# Revit family: HOSPIVAC V3 E65-300
name_source: partatom
category: Equipement de génie climatique
revit_build: Autodesk Revit 2018 (Build: 20170223_1515(x64)
units: mm (PartAtom-declared; Revit-internal decimal feet)

## family parameters
Basée sur le plan de construction = Non
Classification = Aucun
Cote de connecteur circulaire = Utiliser le diamètre
Couper avec des vides une fois chargée = Non
Partagée = Non
Point de calcul de pièce = Non
Toujours verticalement = Oui
Type d'élément = Normal

## types (5) — shared parameters
COS_PHI = 0.9
DIAM_ASPI_VIDE = 32 mm  [stored 0.104987 ft]
DIAM_REFOUL_VIDE = 40 mm  [stored 0.131234 ft]
DOUBLE_ALIMENTATION = Oui
FREQUENCE = 50 Hz
Fabricant = MIL'S
Lien espace client = https://www.mils.fr
Modèle = HOSPIVAC V3 EVISA
NBR_POLES = 3
NEUTRE = Oui
OFFSET_HAUT_ASPI = 895 mm  [stored 2.93635 ft]
OFFSET_HAUT_REFOUL = 410 mm  [stored 1.34514 ft]
TENSION_ALIM = 400 V
TERRE = Oui
Zone de maintenance 1 = Oui

## per-type parameters (varying)
- a - HOSPIVAC V3 E65: DEBIT_ASPI_VIDE=204.0 m³/h; DEBIT_REFOUL_VIDE=204.0 m³/h; DEGAG_CALORIFIQUE(kJ/h)=18604; DESCR_ALIM_X=Alimentation X ; 5G1.5mm²; DESCR_ALIM_Y=Alimentation Y ; 5G1.5mm²; DESCR_ASPI=Aspiration Vide ; 3x68 m³/h ; G 1"1/4 FEM; DESCR_REFOUL=Refoulement Vide ; 3x68 m³/h ; G 1"1/2 MAL; DESCR_RESERV=Aspiration Réservoir ; G 1"1/4 FEM; HAUTEUR=1835 mm; HAUTEUR_AVEC_POTENCE=2250 mm; LARGEUR=705 mm  [stored 2.31299 ft]; LONGUEUR=1405 mm  [stored 4.60958 ft]; NIVEAU_SONORE(dB(A))=67; OFFSET_HAUT_PPE_A=225.5 mm; OFFSET_HAUT_PPE_B=831 mm; OFFSET_HAUT_PPE_C=1445 mm; OFFSET_HAUT_RESERV=1200 mm  [stored 3.93701 ft]; OFFSET_LARG_MAINT=947 mm  [stored 3.10696 ft]; OFFSET_LARG_PPE=130 mm  [stored 0.426509 ft]; OFFSET_LARG_REFOUL=312.5 mm  [stored 1.02526 ft]; OFFSET_LARG_RESERV=345 mm  [stored 1.13189 ft]; OFFSET_LONG_ASPI=1215 mm  [stored 3.98622 ft]; OFFSET_LONG_MAINT=1300 mm  [stored 4.26509 ft]; OFFSET_LONG_PPE=731 mm; OFFSET_LONG_REFOUL=975 mm  [stored 3.19882 ft]; OFFSET_LONG_RESERV=930 mm  [stored 3.05118 ft]; POIDS(Kg)=460 mm  [stored 1.50919 ft]; PROTEC_ELECT_X=Disjoncteur courbe D - 6 A; PROTEC_ELECT_Y=Disjoncteur courbe D - 10 A; PUISS_APPARENTE_X=1667 VA; PUISS_APPARENTE_Y=3333 VA; PUISS_ELECT_X=2 kW; PUISS_ELECT_Y=3 kW; TYPE CHASSIS=CHASSIS HOSPIVAC EVISA V3 E65-300 : CHASSIS V3 E65-100; TYPE_PPE=EVISA : e - E65.R
- b - HOSPIVAC V3 E100: DEBIT_ASPI_VIDE=300.0 m³/h; DEBIT_REFOUL_VIDE=300.0 m³/h; DEGAG_CALORIFIQUE(kJ/h)=27286; DESCR_ALIM_X=Alimentation X ; 5G1.5mm²; DESCR_ALIM_Y=Alimentation Y ; 5G2.5mm²; DESCR_ASPI=Aspiration Vide ; 3x100 m³/h ; G 1"1/4 FEM; DESCR_REFOUL=Refoulement Vide ; 3x100 m³/h ; G 1"1/2 MAL; DESCR_RESERV=Aspiration Réservoir ; G 1"1/4 FEM; HAUTEUR=1835 mm; HAUTEUR_AVEC_POTENCE=2250 mm; LARGEUR=705 mm  [stored 2.31299 ft]; LONGUEUR=1405 mm  [stored 4.60958 ft]; NIVEAU_SONORE(dB(A))=67; OFFSET_HAUT_PPE_A=225.5 mm; OFFSET_HAUT_PPE_B=831 mm; OFFSET_HAUT_PPE_C=1445 mm; OFFSET_HAUT_RESERV=1200 mm  [stored 3.93701 ft]; OFFSET_LARG_MAINT=1020.9 mm; OFFSET_LARG_PPE=130 mm  [stored 0.426509 ft]; OFFSET_LARG_REFOUL=312.5 mm  [stored 1.02526 ft]; OFFSET_LARG_RESERV=347 mm  [stored 1.13845 ft]; OFFSET_LONG_ASPI=1215 mm  [stored 3.98622 ft]; OFFSET_LONG_MAINT=2030 mm; OFFSET_LONG_PPE=731 mm; OFFSET_LONG_REFOUL=975 mm  [stored 3.19882 ft]; OFFSET_LONG_RESERV=930 mm  [stored 3.05118 ft]; POIDS(Kg)=470 mm  [stored 1.54199 ft]; PROTEC_ELECT_X=Disjoncteur courbe D - 10 A; PROTEC_ELECT_Y=Disjoncteur courbe D - 16 A; PUISS_APPARENTE_X=2444 VA; PUISS_APPARENTE_Y=4889 VA; PUISS_ELECT_X=2 kW; PUISS_ELECT_Y=4 kW; TYPE CHASSIS=CHASSIS HOSPIVAC EVISA V3 E65-300 : CHASSIS V3 E65-100; TYPE_PPE=EVISA : f - E100.R
- c - HOSPIVAC V3 E150: DEBIT_ASPI_VIDE=396.0 m³/h; DEBIT_REFOUL_VIDE=396.0 m³/h; DEGAG_CALORIFIQUE(kJ/h)=37208; DESCR_ALIM_X=Alimentation X ; 5G2.5mm²; DESCR_ALIM_Y=Alimentation Y ; 5G2.5mm²; DESCR_ASPI=Aspiration Vide ; 3x150 m³/h ; G 2" FEM; DESCR_REFOUL=Refoulement Vide ; 3x150 m³/h ; G 2" MAL; DESCR_RESERV=Aspiration Réservoir ; G 2" FEM; HAUTEUR=2075 mm; HAUTEUR_AVEC_POTENCE=2430 mm; LARGEUR=795 mm  [stored 2.60827 ft]; LONGUEUR=2280 mm; NIVEAU_SONORE(dB(A))=69; OFFSET_HAUT_PPE_A=256 mm  [stored 0.839895 ft]; OFFSET_HAUT_PPE_B=926 mm  [stored 3.03806 ft]; OFFSET_HAUT_PPE_C=1591 mm  [stored 5.21982 ft]; OFFSET_HAUT_RESERV=1330 mm  [stored 4.36352 ft]; OFFSET_LARG_MAINT=1020.9 mm; OFFSET_LARG_PPE=200 mm  [stored 0.656168 ft]; OFFSET_LARG_REFOUL=347.5 mm  [stored 1.14009 ft]; OFFSET_LARG_RESERV=400 mm  [stored 1.31234 ft]; OFFSET_LONG_ASPI=1530 mm  [stored 5.01969 ft]; OFFSET_LONG_MAINT=2030 mm; OFFSET_LONG_PPE=731 mm; OFFSET_LONG_REFOUL=1294 mm  [stored 4.24541 ft]; OFFSET_LONG_RESERV=1220 mm  [stored 4.00262 ft]; POIDS(Kg)=670 mm  [stored 2.19816 ft]; PROTEC_ELECT_X=Disjoncteur courbe D - 10 A; PROTEC_ELECT_Y=Disjoncteur courbe D - 16 A; PUISS_APPARENTE_X=3333 VA; PUISS_APPARENTE_Y=6667 VA; PUISS_ELECT_X=3 kW; PUISS_ELECT_Y=6 kW; TYPE CHASSIS=CHASSIS HOSPIVAC EVISA V3 E65-300 : CHASSIS V3 E150-300; TYPE_PPE=EVISA : g - E150.R
- d - HOSPIVAC V3 E200: DEBIT_ASPI_VIDE=600.0 m³/h; DEBIT_REFOUL_VIDE=600.0 m³/h; DEGAG_CALORIFIQUE(kJ/h)=49611; DESCR_ALIM_X=Alimentation X ; 5G2.5mm²; DESCR_ALIM_Y=Alimentation Y ; 5G4mm²; DESCR_ASPI=Aspiration Vide ; 3x200 m³/h ; G 2" FEM; DESCR_REFOUL=Refoulement Vide ; 3x200 m³/h ; G 2" MAL; DESCR_RESERV=Aspiration Réservoir ; G 2" FEM; HAUTEUR=2075 mm; HAUTEUR_AVEC_POTENCE=2430 mm; LARGEUR=795 mm  [stored 2.60827 ft]; LONGUEUR=2280 mm; NIVEAU_SONORE(dB(A))=72; OFFSET_HAUT_PPE_A=256 mm  [stored 0.839895 ft]; OFFSET_HAUT_PPE_B=926 mm  [stored 3.03806 ft]; OFFSET_HAUT_PPE_C=1591 mm  [stored 5.21982 ft]; OFFSET_HAUT_RESERV=1330 mm  [stored 4.36352 ft]; OFFSET_LARG_MAINT=1150 mm; OFFSET_LARG_PPE=200 mm  [stored 0.656168 ft]; OFFSET_LARG_REFOUL=347.5 mm  [stored 1.14009 ft]; OFFSET_LARG_RESERV=400 mm  [stored 1.31234 ft]; OFFSET_LONG_ASPI=1530 mm  [stored 5.01969 ft]; OFFSET_LONG_MAINT=1810 mm; OFFSET_LONG_PPE=700 mm  [stored 2.29659 ft]; OFFSET_LONG_REFOUL=1294 mm  [stored 4.24541 ft]; OFFSET_LONG_RESERV=1220 mm  [stored 4.00262 ft]; POIDS(Kg)=744 mm  [stored 2.44094 ft]; PROTEC_ELECT_X=Disjoncteur courbe D - 16 A; PROTEC_ELECT_Y=Disjoncteur courbe D - 25 A; PUISS_APPARENTE_X=4444 VA; PUISS_APPARENTE_Y=8889 VA; PUISS_ELECT_X=4 kW; PUISS_ELECT_Y=8 kW; TYPE CHASSIS=CHASSIS HOSPIVAC EVISA V3 E65-300 : CHASSIS V3 E150-300; TYPE_PPE=EVISA : h - E200.R
- e - HOSPIVAC V3 E300: DEBIT_ASPI_VIDE=900.0 m³/h; DEBIT_REFOUL_VIDE=900.0 m³/h; DEGAG_CALORIFIQUE(kJ/h)=66148; DESCR_ALIM_X=Alimentation X ; 5G2.5mm²; DESCR_ALIM_Y=Alimentation Y ; 5G6mm²; DESCR_ASPI=Aspiration Vide ; 3x300 m³/h ; G 2" FEM; DESCR_REFOUL=Refoulement Vide ; 3x300 m³/h ; G 2" MAL; DESCR_RESERV=Aspiration Réservoir ; G 2" FEM; HAUTEUR=2090 mm; HAUTEUR_AVEC_POTENCE=2430 mm; LARGEUR=795 mm  [stored 2.60827 ft]; LONGUEUR=1745 mm; NIVEAU_SONORE(dB(A))=72; OFFSET_HAUT_PPE_A=256 mm  [stored 0.839895 ft]; OFFSET_HAUT_PPE_B=926 mm  [stored 3.03806 ft]; OFFSET_HAUT_PPE_C=1591 mm  [stored 5.21982 ft]; OFFSET_HAUT_RESERV=1330 mm  [stored 4.36352 ft]; OFFSET_LARG_MAINT=1020.9 mm; OFFSET_LARG_PPE=200 mm  [stored 0.656168 ft]; OFFSET_LARG_REFOUL=347.5 mm  [stored 1.14009 ft]; OFFSET_LARG_RESERV=400 mm  [stored 1.31234 ft]; OFFSET_LONG_ASPI=1530 mm  [stored 5.01969 ft]; OFFSET_LONG_MAINT=2030 mm; OFFSET_LONG_PPE=740 mm  [stored 2.42782 ft]; OFFSET_LONG_REFOUL=1294 mm  [stored 4.24541 ft]; OFFSET_LONG_RESERV=1220 mm  [stored 4.00262 ft]; POIDS(Kg)=833 mm  [stored 2.73294 ft]; PROTEC_ELECT_X=Disjoncteur courbe D - 20 A; PROTEC_ELECT_Y=Disjoncteur courbe D - 32 A; PUISS_APPARENTE_X=6111 VA; PUISS_APPARENTE_Y=12222 VA; PUISS_ELECT_X=6 kW; PUISS_ELECT_Y=11 kW; TYPE CHASSIS=CHASSIS HOSPIVAC EVISA V3 E65-300 : CHASSIS V3 E150-300; TYPE_PPE=EVISA : i - E300.R

note: [stored X ft] marks values corroborated as IEEE doubles in the binary element streams (Revit-internal decimal feet)

## geometry (parser evidence)
native form markers: Sweep x2
no freeform markers — native parametric forms only
